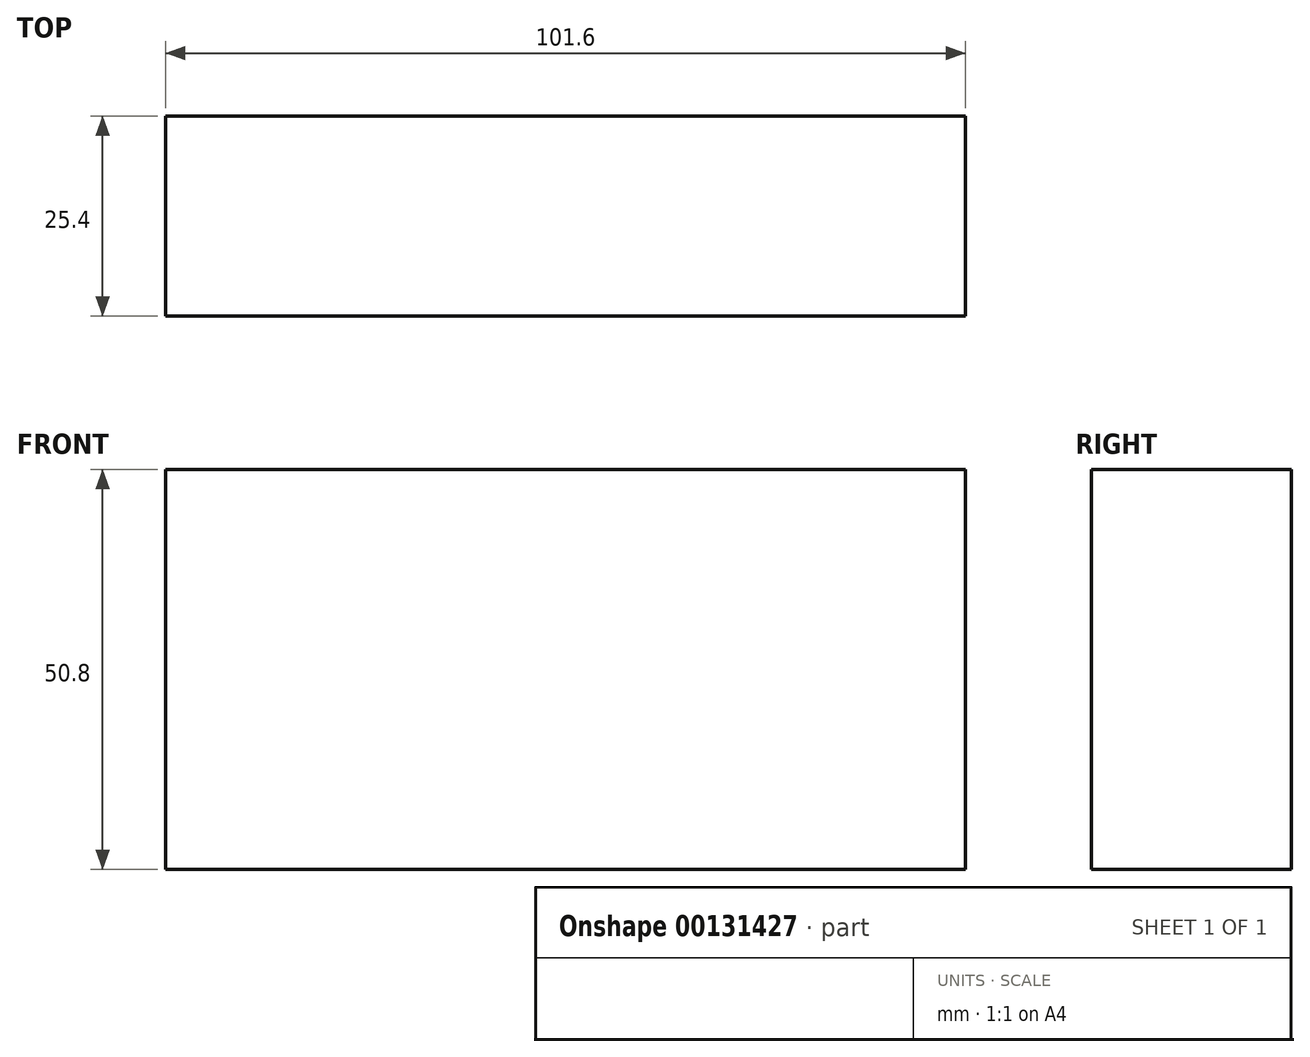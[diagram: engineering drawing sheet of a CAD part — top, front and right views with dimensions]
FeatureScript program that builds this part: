
annotation { "Feature Type Name" : "Feature", "Feature Type Description" : "" }
export const myFeature = defineFeature(function(context is Context, id is Id, definition is map)
    precondition{}
    {
        {
            var Q0;
            Q0=qCreatedBy(makeId("Front.planeOp"),FACE);
            var sketch = newSketch(context, id + "F0", { "sketchPlane" : qUnion([Q0])});
            skLineSegment(sketch, "E0.bottom", {"start": v(50.8, 25.4) * mm, "end": v(-50.8, 25.4) * mm});
            skLineSegment(sketch, "E0.top", {"start": v(50.8, -25.4) * mm, "end": v(-50.8, -25.4) * mm});
            skLineSegment(sketch, "E0.left", {"start": v(50.8, 25.4) * mm, "end": v(50.8, -25.4) * mm});
            skLineSegment(sketch, "E0.right", {"start": v(-50.8, 25.4) * mm, "end": v(-50.8, -25.4) * mm});
            skPoint(sketch, "E0.middle", {"position": v(0, 0) * mm});
            skSolve(sketch);
        }
        {
            var Q0;
            Q0 = qSketchRegion(id + "F0", true);
            var Q1;
            Q1=makeQuery(id+"F0.imprint","IMPRINT",FACE,{"disambiguationData":[TD([[makeQuery(id+"F0.imprint","IMPRINT",EDGE,{"derivedFrom":sQuery(id+"F0.wireOp",EDGE,"E0.bottom")}),1.0]])]});
            extrude(context, id + "F1", {"entities" : qUnion([Q0, Q1]), "depth" : 25.4 * mm});
        }
    });
